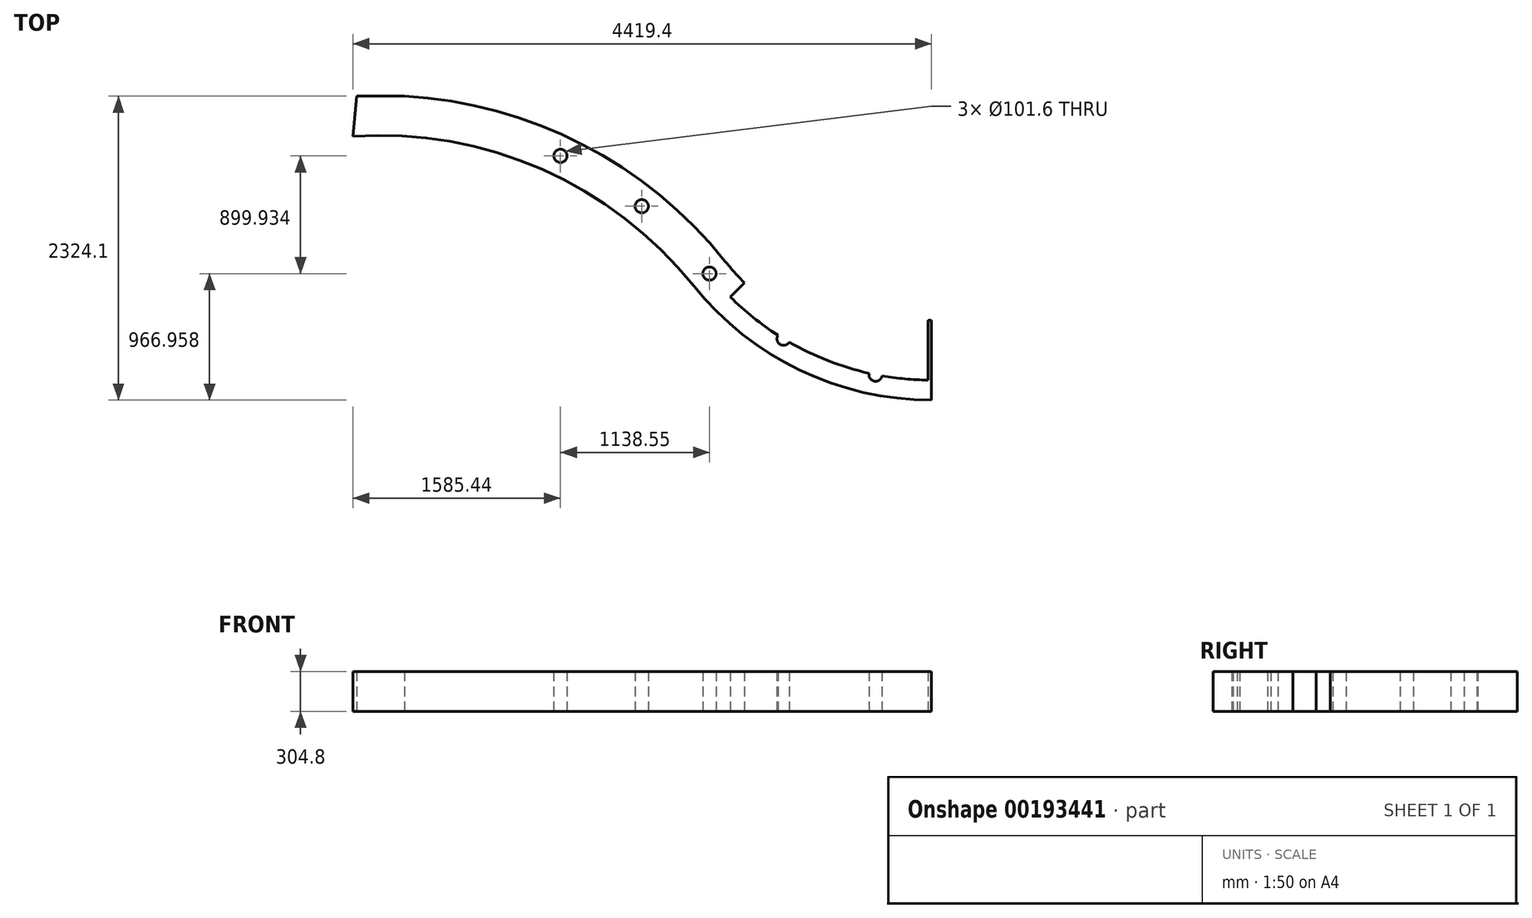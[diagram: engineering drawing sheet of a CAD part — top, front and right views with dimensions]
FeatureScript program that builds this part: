
annotation { "Feature Type Name" : "Feature", "Feature Type Description" : "" }
export const myFeature = defineFeature(function(context is Context, id is Id, definition is map)
    precondition{}
    {
        {
            var Q0;
            Q0=qCreatedBy(makeId("Top.planeOp"),FACE);
            var sketch = newSketch(context, id + "F0", { "sketchPlane" : qUnion([Q0])});
            skLineSegment(sketch, "E0", {"start": v(-2322.3, 99.74) * mm, "end": v(363.78, 99.74) * mm});
            skLineSegment(sketch, "E1", {"start": v(2078.28, -1614.76) * mm, "end": v(2078.28, -2224.36) * mm});
            skArc(sketch, "E2", {"start": v(2078.28, -1614.76) * mm, "mid": v(865.95, -1112.6) * mm, "end": v(363.78, 99.74) * mm});
            skArc(sketch, "E3.0", {"start": v(2078.28, -1919.56) * mm, "mid": v(1203.8, -1720.4) * mm, "end": v(501.84, -1162.16) * mm});
            skArc(sketch, "E4.0", {"start": v(2078.28, -2224.36) * mm, "mid": v(1071.81, -1995.13) * mm, "end": v(263.88, -1352.64) * mm});
            skLineSegment(sketch, "E5", {"start": v(-2322.3, 99.74) * mm, "end": v(-2341.12, -206.78) * mm});
            skPoint(sketch, "E6", {"position": v(-2322.3, 99.74) * mm});
            skArc(sketch, "E7", {"start": v(501.84, -1162.16) * mm, "mid": v(-757.31, -188.98) * mm, "end": v(-2322.3, 99.74) * mm});
            skArc(sketch, "E8.0", {"start": v(263.88, -1352.64) * mm, "mid": v(-898, -460.02) * mm, "end": v(-2341.12, -206.78) * mm});
            skPoint(sketch, "E9.orphan", {"position": v(-2399.79, -1162.16) * mm});
            skLineSegment(sketch, "E10", {"start": v(2078.28, 99.74) * mm, "end": v(0, -1978.55) * mm});
            skLineSegment(sketch, "E11", {"start": v(-2341.12, -206.78) * mm, "end": v(-2322.3, 99.74) * mm});
            skLineSegment(sketch, "E12", {"start": v(2078.28, -1614.76) * mm, "end": v(2052.9, -1614.09) * mm});
            skLineSegment(sketch, "E13.0", {"start": v(2052.88, -1614.09) * mm, "end": v(2052.88, -2223.26) * mm});
            skLineSegment(sketch, "E14", {"start": v(-2339.55, -181.22) * mm, "end": v(-2322.3, 99.74) * mm});
            skLineSegment(sketch, "E15", {"start": v(-2341.12, -206.78) * mm, "end": v(-2314.2, 100.17) * mm});
            skArc(sketch, "E16.0", {"start": v(739.8, -971.69) * mm, "mid": v(106.57, -351.34) * mm, "end": v(-656.54, 99.74) * mm});
            skPoint(sketch, "E17", {"position": v(501.84, -1162.16) * mm});
            skPoint(sketch, "E18", {"position": v(-40.64, -623.01) * mm});
            skPoint(sketch, "E19", {"position": v(-690.5, -219.71) * mm});
            skLineSegment(sketch, "E20", {"start": v(-690.5, -219.71) * mm, "end": v(-2135.43, -3273.22) * mm, "construction": true});
            skLineSegment(sketch, "E21", {"start": v(-40.64, -623.01) * mm, "end": v(-2135.43, -3273.22) * mm, "construction": true});
            skLineSegment(sketch, "E22", {"start": v(501.84, -1162.16) * mm, "end": v(-2135.43, -3273.22) * mm, "construction": true});
            skLineSegment(sketch, "E23", {"start": v(2078.28, 99.74) * mm, "end": v(2078.28, -2195.86) * mm, "construction": true});
            skPoint(sketch, "E24", {"position": v(1028.5, -1625.24) * mm});
            skPoint(sketch, "E25", {"position": v(1681.79, -1880.26) * mm});
            skLineSegment(sketch, "E26", {"start": v(2078.28, 99.74) * mm, "end": v(501.84, -1162.16) * mm, "construction": true});
            skLineSegment(sketch, "E27", {"start": v(2078.28, 99.74) * mm, "end": v(870.05, -1885.61) * mm, "construction": true});
            skLineSegment(sketch, "E28", {"start": v(2078.28, 99.74) * mm, "end": v(1621.94, -2179.12) * mm, "construction": true});
            skArc(sketch, "E29.0", {"start": v(382.86, -1257.4) * mm, "mid": v(-819.48, -328.12) * mm, "end": v(-2313.87, -52.43) * mm});
            skArc(sketch, "E30.0", {"start": v(2078.28, -2071.96) * mm, "mid": v(1137.8, -1857.76) * mm, "end": v(382.86, -1257.4) * mm});
            skCircle(sketch, "E31", {"center": v(-755.68, -357.47) * mm, "radius": 50.8 * mm});
            skCircle(sketch, "E32", {"center": v(-135.14, -742.57) * mm, "radius": 50.8 * mm});
            skCircle(sketch, "E33", {"center": v(382.86, -1257.4) * mm, "radius": 50.8 * mm});
            skCircle(sketch, "E34", {"center": v(949.28, -1755.43) * mm, "radius": 50.8 * mm});
            skCircle(sketch, "E35", {"center": v(1651.86, -2029.69) * mm, "radius": 50.8 * mm});
            skPoint(sketch, "E36", {"position": v(-1941.3, 99.74) * mm});
            skPoint(sketch, "E37", {"position": v(-841.48, 99.74) * mm});
            skPoint(sketch, "E38", {"position": v(-1391.39, 99.74) * mm});
            skSolve(sketch);
        }
        {
            var Q0;
            {var subQ9=sQuery(id+"F0.wireOp",EDGE,"E8.0");Q0=makeQuery(id+"F0.imprint","IMPRINT",FACE,{"disambiguationData":[TD([[makeQuery(id+"F0.imprint","IMPRINT",EDGE,{"derivedFrom":subQ9}),-1.0]])]});}
            extrude(context, id + "F1", {"entities" : qUnion([Q0]), "depth" : 304.8 * mm});
        }
        {
            var Q0;
            {var subQ0=sQuery(id+"F0.wireOp",EDGE,"E4.0");var subQ1=sQuery(id+"F0.wireOp",EDGE,"E1");var subQ2=makeQuery(id+"F0.imprint","INTERSECT",VERTEX,{"derivedFrom":[subQ1,subQ0]});Q0=makeQuery(id+"F0.imprint","IMPRINT",FACE,{"disambiguationData":[TD([[makeQuery(id+"F0.imprint","IMPRINT",EDGE,{"disambiguationData":[TD([[subQ2,1.0]])],"derivedFrom":subQ1}),-1.0]])]});}
            extrude(context, id + "F2", {"entities" : qUnion([Q0]), "operationType" : NewBodyOperationType.ADD, "depth" : 304.8 * mm});
        }
        {
            var Q0;
            {var subQ1=sQuery(id+"F0.wireOp",EDGE,"E13.0");var subQ3=sQuery(id+"F0.wireOp",EDGE,"E3.0");var subQ4=makeQuery(id+"F0.imprint","INTERSECT",VERTEX,{"derivedFrom":[subQ3,subQ1]});Q0=makeQuery(id+"F0.imprint","IMPRINT",FACE,{"disambiguationData":[TD([[makeQuery(id+"F0.imprint","IMPRINT",EDGE,{"disambiguationData":[TD([[subQ4,-1.0]])],"derivedFrom":subQ3}),1.0]])]});}
            var Q1;
            {var subQ0=sQuery(id+"F0.wireOp",EDGE,"E3.0");var subQ1=sQuery(id+"F0.wireOp",EDGE,"E1");var subQ2=makeQuery(id+"F0.imprint","INTERSECT",VERTEX,{"derivedFrom":[subQ1,subQ0]});Q1=makeQuery(id+"F0.imprint","IMPRINT",FACE,{"disambiguationData":[TD([[makeQuery(id+"F0.imprint","IMPRINT",EDGE,{"disambiguationData":[TD([[subQ2,-1.0]])],"derivedFrom":subQ1}),-1.0]])]});}
            extrude(context, id + "F3", {"entities" : qUnion([Q0, Q1]), "operationType" : NewBodyOperationType.ADD, "depth" : 304.8 * mm});
        }
    });
